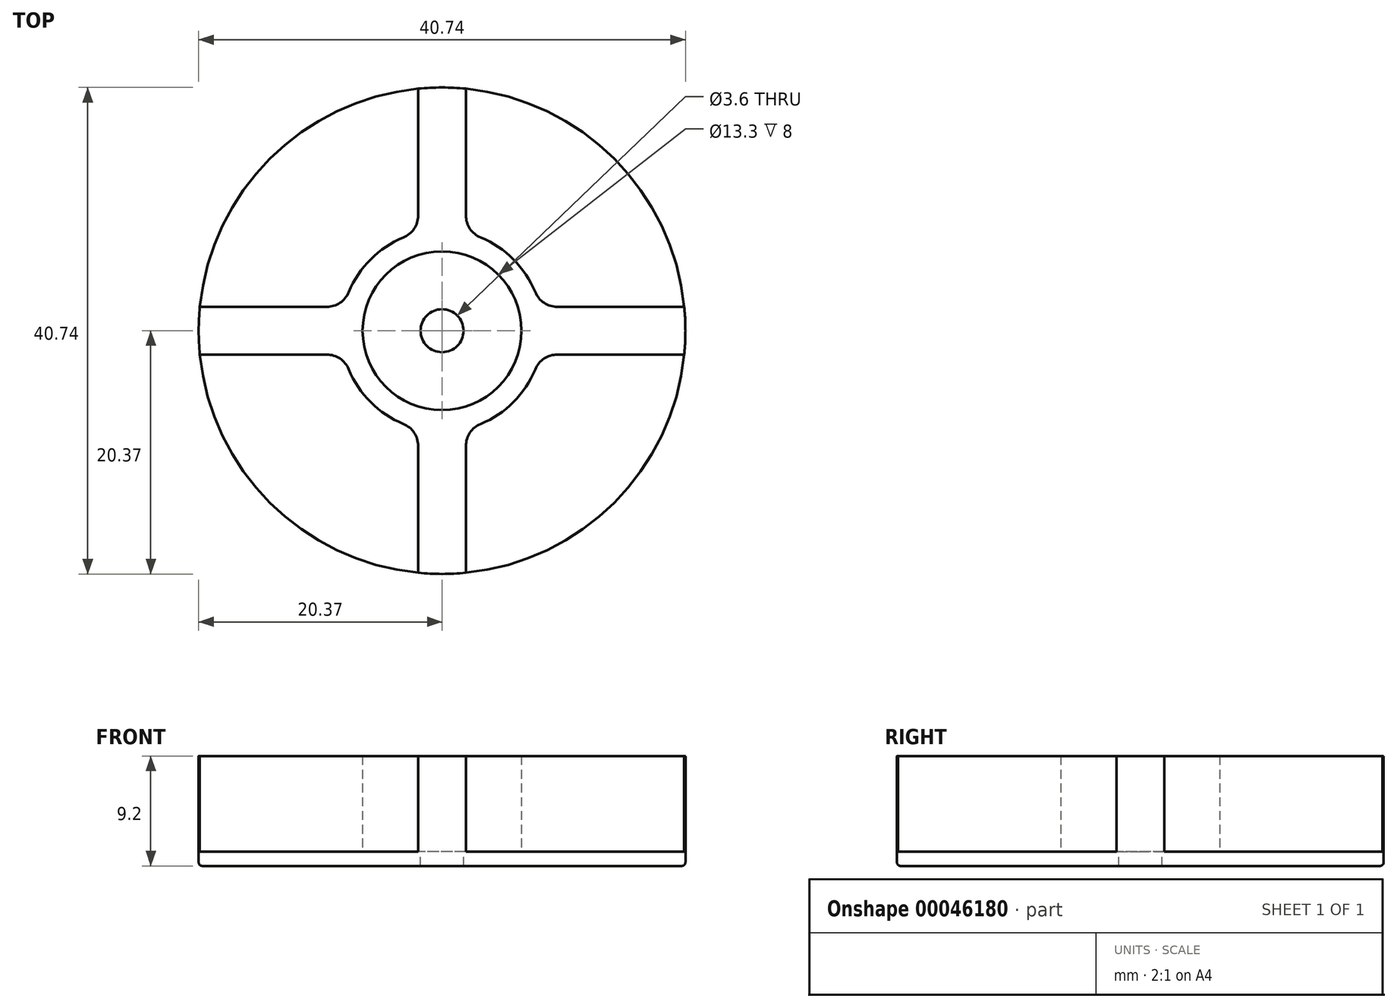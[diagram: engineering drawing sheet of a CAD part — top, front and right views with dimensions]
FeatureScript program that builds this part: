
annotation { "Feature Type Name" : "Feature", "Feature Type Description" : "" }
export const myFeature = defineFeature(function(context is Context, id is Id, definition is map)
    precondition{}
    {
        {
            var Q0;
            Q0=qCreatedBy(makeId("Top.planeOp"),FACE);
            var sketch = newSketch(context, id + "F0", { "sketchPlane" : qUnion([Q0])});
            skCircle(sketch, "E0", {"center": v(0, 0) * mm, "radius": 20.37 * mm});
            skLineSegment(sketch, "E1", {"start": v(0, 0) * mm, "end": v(0, 20.37) * mm, "construction": true});
            skLineSegment(sketch, "E2", {"start": v(0, 0) * mm, "end": v(2, 20.27) * mm, "construction": true});
            skLineSegment(sketch, "E3", {"start": v(7.8, 18.82) * mm, "end": v(0, 0) * mm, "construction": true});
            skLineSegment(sketch, "E4", {"start": v(0, 0) * mm, "end": v(14.4, 14.4) * mm, "construction": true});
            skLineSegment(sketch, "E5", {"start": v(2, 20.27) * mm, "end": v(2, 9.65) * mm});
            skLineSegment(sketch, "E6", {"start": v(0, 0) * mm, "end": v(3.97, 19.98) * mm, "construction": true});
            skLineSegment(sketch, "E7.MirrorCS", {"start": v(20.27, 2) * mm, "end": v(9.65, 2) * mm});
            skPoint(sketch, "E8.newPointA", {"position": v(-1.41, 1.41) * mm});
            skPoint(sketch, "E8.newPointB", {"position": v(2, 0) * mm});
            skArc(sketch, "E8.filletArc", {"start": v(2, 9.65) * mm, "mid": v(2.34, 8.54) * mm, "end": v(3.23, 7.8) * mm});
            skPoint(sketch, "E9.newPointA", {"position": v(1.41, -1.41) * mm});
            skPoint(sketch, "E9.newPointB", {"position": v(0, 2) * mm});
            skArc(sketch, "E9.filletArc", {"start": v(7.8, 3.23) * mm, "mid": v(8.54, 2.34) * mm, "end": v(9.65, 2) * mm});
            skLineSegment(sketch, "E10.MirrorCS", {"start": v(20.27, -2) * mm, "end": v(9.65, -2) * mm});
            skArc(sketch, "E11.MirrorCS", {"start": v(7.8, -3.23) * mm, "mid": v(8.54, -2.34) * mm, "end": v(9.65, -2) * mm});
            skArc(sketch, "E12.MirrorCS", {"start": v(2, -9.65) * mm, "mid": v(2.34, -8.54) * mm, "end": v(3.23, -7.8) * mm});
            skLineSegment(sketch, "E13.MirrorCS", {"start": v(2, -20.27) * mm, "end": v(2, -9.65) * mm});
            skLineSegment(sketch, "E14.MirrorCS", {"start": v(-2, 20.27) * mm, "end": v(-2, 9.65) * mm});
            skArc(sketch, "E15.MirrorCS", {"start": v(-2, 9.65) * mm, "mid": v(-2.34, 8.54) * mm, "end": v(-3.23, 7.8) * mm});
            skArc(sketch, "E16.MirrorCS", {"start": v(-7.8, 3.23) * mm, "mid": v(-8.54, 2.34) * mm, "end": v(-9.65, 2) * mm});
            skLineSegment(sketch, "E17.MirrorCS", {"start": v(-20.27, 2) * mm, "end": v(-9.65, 2) * mm});
            skLineSegment(sketch, "E18.MirrorCS", {"start": v(-20.27, -2) * mm, "end": v(-9.65, -2) * mm});
            skArc(sketch, "E19.MirrorCS", {"start": v(-7.8, -3.23) * mm, "mid": v(-8.54, -2.34) * mm, "end": v(-9.65, -2) * mm});
            skArc(sketch, "E20.MirrorCS", {"start": v(-2, -9.65) * mm, "mid": v(-2.34, -8.54) * mm, "end": v(-3.23, -7.8) * mm});
            skLineSegment(sketch, "E21.MirrorCS", {"start": v(-2, -20.27) * mm, "end": v(-2, -9.65) * mm});
            skCircle(sketch, "E22.0", {"center": v(0, 0) * mm, "radius": 6.65 * mm});
            skArc(sketch, "E23", {"start": v(-1, -1.12) * mm, "mid": v(1.5, 0) * mm, "end": v(-1, 1.12) * mm, "construction": true});
            skLineSegment(sketch, "E24", {"start": v(-1, 1.12) * mm, "end": v(-1, -1.12) * mm, "construction": true});
            skArc(sketch, "E25", {"start": v(-3.23, 7.8) * mm, "mid": v(-5.97, 5.97) * mm, "end": v(-7.8, 3.23) * mm});
            skPoint(sketch, "E26.orphan", {"position": v(-5.41, 8.24) * mm});
            skPoint(sketch, "E27.MirrorCS.start.orphan", {"position": v(-12.92, 15.75) * mm});
            skPoint(sketch, "E28.MirrorCS.end.orphan", {"position": v(-8.24, 5.41) * mm});
            skPoint(sketch, "E28.MirrorCS.start.orphan", {"position": v(-15.75, 12.92) * mm});
            skPoint(sketch, "E29.MirrorCS.end.orphan", {"position": v(5.41, 8.24) * mm});
            skPoint(sketch, "E29.MirrorCS.start.orphan", {"position": v(12.92, 15.75) * mm});
            skPoint(sketch, "E30.MirrorCS.end.orphan", {"position": v(-8.24, -5.41) * mm});
            skPoint(sketch, "E30.MirrorCS.start.orphan", {"position": v(-15.75, -12.92) * mm});
            skPoint(sketch, "E31.MirrorCS.end.orphan", {"position": v(-5.41, -8.24) * mm});
            skPoint(sketch, "E31.MirrorCS.start.orphan", {"position": v(-12.92, -15.75) * mm});
            skArc(sketch, "E32.trimOffspring", {"start": v(-7.8, -3.23) * mm, "mid": v(-5.97, -5.97) * mm, "end": v(-3.23, -7.8) * mm});
            skArc(sketch, "E33.trimOffspring", {"start": v(3.23, -7.8) * mm, "mid": v(5.97, -5.97) * mm, "end": v(7.8, -3.23) * mm});
            skPoint(sketch, "E34.orphan", {"position": v(5.41, -8.24) * mm});
            skPoint(sketch, "E35.MirrorCS.start.orphan", {"position": v(12.92, -15.75) * mm});
            skPoint(sketch, "E36.orphan", {"position": v(8.24, -5.41) * mm});
            skPoint(sketch, "E37.MirrorCS.start.orphan", {"position": v(15.75, -12.92) * mm});
            skPoint(sketch, "E38.MirrorCS.end.orphan", {"position": v(8.24, 5.41) * mm});
            skPoint(sketch, "E38.MirrorCS.start.orphan", {"position": v(15.75, 12.92) * mm});
            skArc(sketch, "E39.trimOffspring", {"start": v(7.8, 3.23) * mm, "mid": v(5.97, 5.97) * mm, "end": v(3.23, 7.8) * mm});
            skCircle(sketch, "E40", {"center": v(0, 0) * mm, "radius": 1.8 * mm});
            skSolve(sketch);
        }
        {
            var Q0;
            {var subQ1=sQuery(id+"F0.wireOp",EDGE,"E7.MirrorCS");Q0=makeQuery(id+"F0.imprint","IMPRINT",FACE,{"disambiguationData":[TD([[makeQuery(id+"F0.imprint","IMPRINT",EDGE,{"derivedFrom":subQ1}),-1.0]])]});}
            var Q1;
            {var subQ1=sQuery(id+"F0.wireOp",EDGE,"E5");Q1=makeQuery(id+"F0.imprint","IMPRINT",FACE,{"disambiguationData":[TD([[makeQuery(id+"F0.imprint","IMPRINT",EDGE,{"derivedFrom":subQ1}),1.0]])]});}
            var Q2;
            {var subQ1=sQuery(id+"F0.wireOp",EDGE,"E14.MirrorCS");Q2=makeQuery(id+"F0.imprint","IMPRINT",FACE,{"disambiguationData":[TD([[makeQuery(id+"F0.imprint","IMPRINT",EDGE,{"derivedFrom":subQ1}),-1.0]])]});}
            var Q3;
            {var subQ1=sQuery(id+"F0.wireOp",EDGE,"E18.MirrorCS");Q3=makeQuery(id+"F0.imprint","IMPRINT",FACE,{"disambiguationData":[TD([[makeQuery(id+"F0.imprint","IMPRINT",EDGE,{"derivedFrom":subQ1}),-1.0]])]});}
            var Q4;
            {var subQ1=sQuery(id+"F0.wireOp",EDGE,"E31.MirrorCS");Q4=makeQuery(id+"F0.imprint","IMPRINT",FACE,{"disambiguationData":[TD([[makeQuery(id+"F0.imprint","IMPRINT",EDGE,{"derivedFrom":subQ1}),-1.0]])]});}
            var Q5;
            {var subQ0=sQuery(id+"F0.wireOp",EDGE,"E35.MirrorCS");Q5=makeQuery(id+"F0.imprint","IMPRINT",FACE,{"disambiguationData":[TD([[makeQuery(id+"F0.imprint","IMPRINT",EDGE,{"derivedFrom":subQ0}),1.0]])]});}
            var Q6;
            {var subQ1=sQuery(id+"F0.wireOp",EDGE,"E10.MirrorCS");Q6=makeQuery(id+"F0.imprint","IMPRINT",FACE,{"disambiguationData":[TD([[makeQuery(id+"F0.imprint","IMPRINT",EDGE,{"derivedFrom":subQ1}),1.0]])]});}
            var Q7;
            {var subQ10=sQuery(id+"F0.wireOp",EDGE,"E5");Q7=makeQuery(id+"F0.imprint","IMPRINT",FACE,{"disambiguationData":[TD([[makeQuery(id+"F0.imprint","IMPRINT",EDGE,{"derivedFrom":subQ10}),-1.0]])]});}
            var Q8;
            {var subQ1=sQuery(id+"F0.wireOp",EDGE,"E28.MirrorCS");Q8=makeQuery(id+"F0.imprint","IMPRINT",FACE,{"disambiguationData":[TD([[makeQuery(id+"F0.imprint","IMPRINT",EDGE,{"derivedFrom":subQ1}),-1.0]])]});}
            var Q9;
            Q9=makeQuery(id+"F0.imprint","IMPRINT",FACE,{"disambiguationData":[TD([[makeQuery(id+"F0.imprint","IMPRINT",EDGE,{"derivedFrom":sQuery(id+"F0.wireOp",EDGE,"E22.0")}),1.0]])]});
            extrude(context, id + "F1", {"entities" : qUnion([Q0, Q1, Q2, Q3, Q4, Q5, Q6, Q7, Q8, Q9]), "oppositeDirection" : true, "depth" : 1.2 * mm});
        }
        {
            var Q0;
            {var subQ10=sQuery(id+"F0.wireOp",EDGE,"E5");Q0=makeQuery(id+"F0.imprint","IMPRINT",FACE,{"disambiguationData":[TD([[makeQuery(id+"F0.imprint","IMPRINT",EDGE,{"derivedFrom":subQ10}),-1.0]])]});}
            extrude(context, id + "F2", {"entities" : qUnion([Q0]), "operationType" : NewBodyOperationType.ADD, "depth" : 8 * mm});
        }
        {
            var Q0;
            Q0=makeQuery(id+"F1.opExtrude","CAP_EDGE",EDGE,{"disambiguationData":[OSD([sQuery(id+"F0.wireOp",EDGE,"E0")])],"isStart":false});
            fillet(context, id + "F3", {"entities" : qUnion([Q0]), "radius" : .3 * mm, "tangentPropagation" : true, "allowEdgeOverflow" : false});
        }
    });
